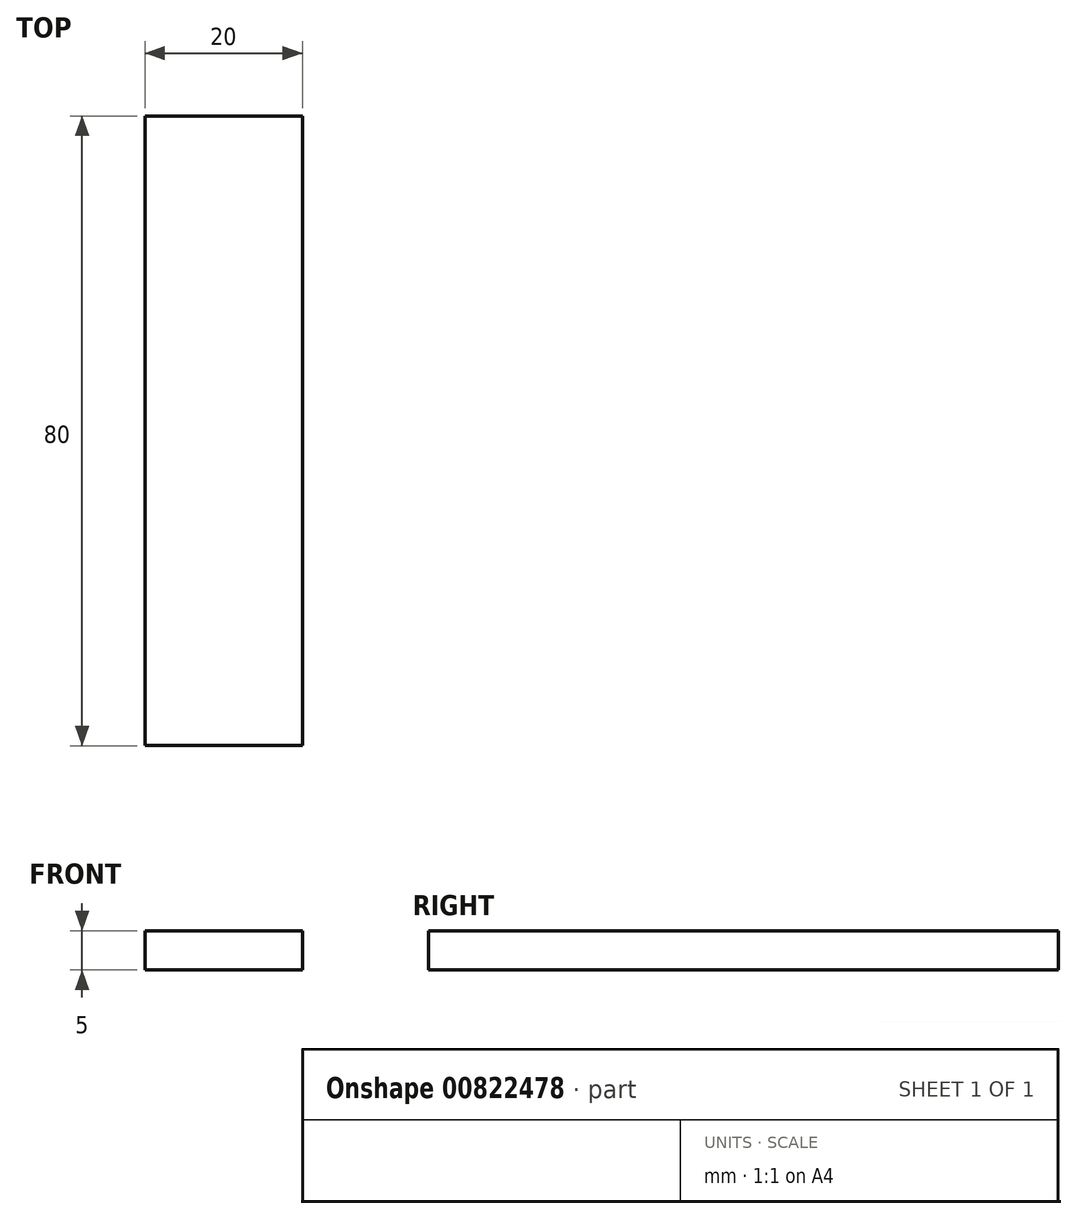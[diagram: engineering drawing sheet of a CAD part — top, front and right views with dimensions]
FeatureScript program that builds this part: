
annotation { "Feature Type Name" : "Feature", "Feature Type Description" : "" }
export const myFeature = defineFeature(function(context is Context, id is Id, definition is map)
    precondition{}
    {
        {
            var Q0;
            Q0=qCreatedBy(makeId("Top.planeOp"),FACE);
            var sketch = newSketch(context, id + "F0", { "sketchPlane" : qUnion([Q0])});
            skLineSegment(sketch, "E0.bottom", {"start": v(-11.06, 31.04) * mm, "end": v(8.94, 31.04) * mm});
            skLineSegment(sketch, "E0.top", {"start": v(-11.06, -48.96) * mm, "end": v(8.94, -48.96) * mm});
            skLineSegment(sketch, "E0.left", {"start": v(-11.06, 31.04) * mm, "end": v(-11.06, -48.96) * mm});
            skLineSegment(sketch, "E0.right", {"start": v(8.94, 31.04) * mm, "end": v(8.94, -48.96) * mm});
            skSolve(sketch);
        }
        {
            var Q0;
            Q0=makeQuery(id+"F0.imprint","IMPRINT",FACE,{"disambiguationData":[TD([[makeQuery(id+"F0.imprint","IMPRINT",EDGE,{"derivedFrom":sQuery(id+"F0.wireOp",EDGE,"E0.bottom")}),-1.0]])]});
            extrude(context, id + "F1", {"entities" : qUnion([Q0]), "depth" : 5 * mm, "offsetDistance" : 25 * mm});
        }
    });
